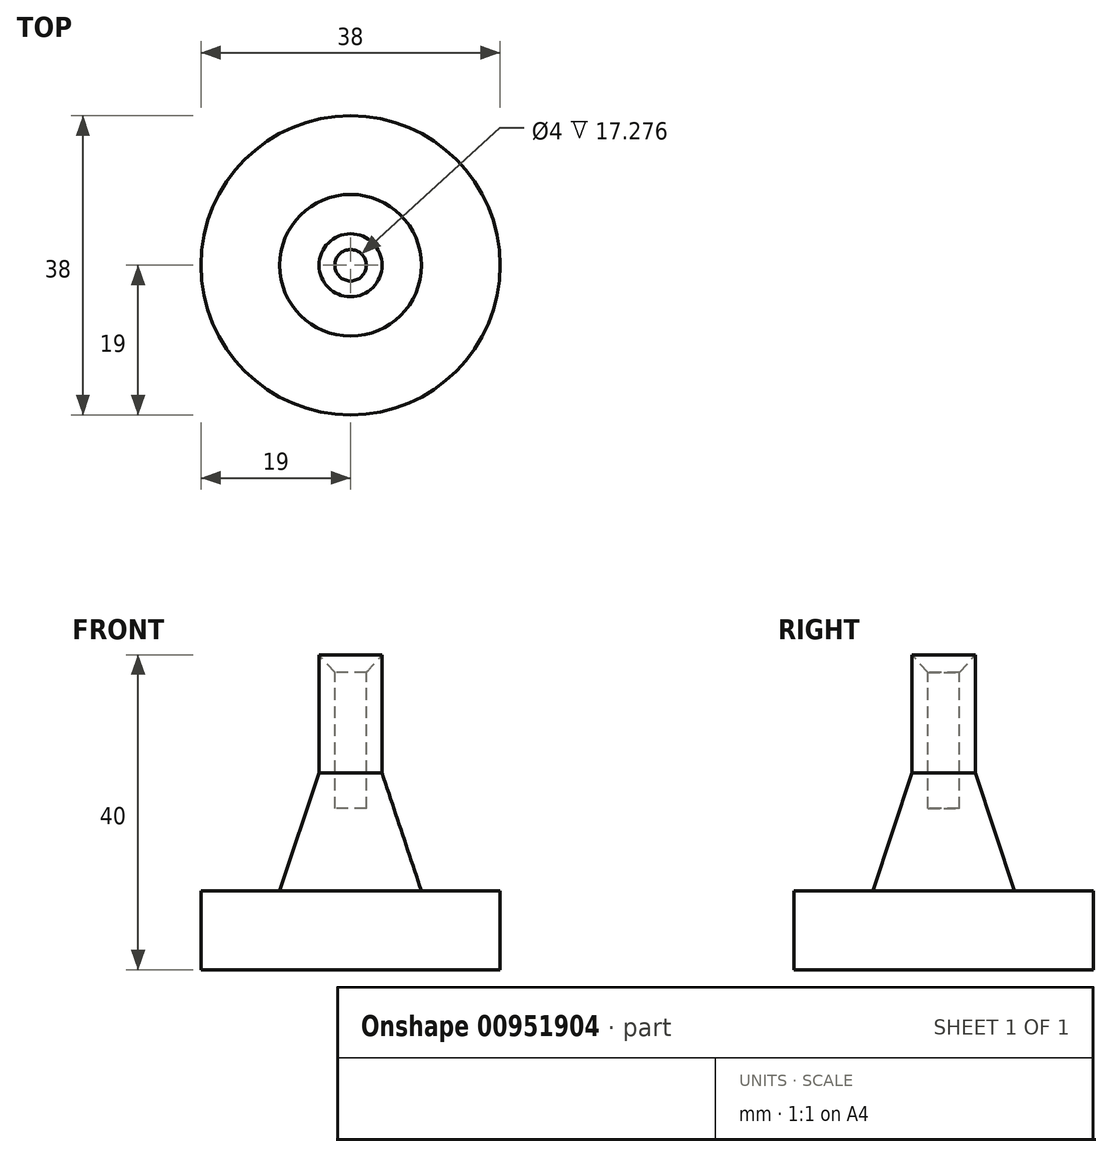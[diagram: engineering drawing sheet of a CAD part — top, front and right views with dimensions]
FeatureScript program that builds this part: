
annotation { "Feature Type Name" : "Feature", "Feature Type Description" : "" }
export const myFeature = defineFeature(function(context is Context, id is Id, definition is map)
    precondition{}
    {
        {
            var Q0;
            Q0=qCreatedBy(makeId("Front.planeOp"),FACE);
            var sketch = newSketch(context, id + "F0", { "sketchPlane" : qUnion([Q0])});
            skLineSegment(sketch, "E0", {"start": v(-4, 35.95) * mm, "end": v(-4, 20.95) * mm});
            skLineSegment(sketch, "E1", {"start": v(-9, 5.95) * mm, "end": v(-19, 5.95) * mm});
            skLineSegment(sketch, "E2", {"start": v(-19, 5.95) * mm, "end": v(-19, -4.05) * mm});
            skLineSegment(sketch, "E3", {"start": v(-19, -4.05) * mm, "end": v(0, -4.05) * mm});
            skLineSegment(sketch, "E4", {"start": v(0, 53.04) * mm, "end": v(0, 35.95) * mm, "construction": true});
            skPoint(sketch, "E4.startSnap0", {"position": v(0, 35.95) * mm});
            skPoint(sketch, "E4.endSnap0", {"position": v(0, -4.05) * mm});
            skPoint(sketch, "E5.end.orphan", {"position": v(4, 35.95) * mm});
            skPoint(sketch, "E6.end.orphan", {"position": v(3, 5.95) * mm});
            skPoint(sketch, "E7.end.orphan", {"position": v(18, 5.95) * mm});
            skPoint(sketch, "E8.orphan", {"position": v(19, -4.05) * mm});
            skLineSegment(sketch, "E9", {"start": v(0, 35.95) * mm, "end": v(0, -4.05) * mm});
            skLineSegment(sketch, "E10", {"start": v(-4, 35.95) * mm, "end": v(-2, 33.71) * mm});
            skLineSegment(sketch, "E11", {"start": v(-2, 33.71) * mm, "end": v(-2, 16.43) * mm});
            skLineSegment(sketch, "E12", {"start": v(-2, 16.43) * mm, "end": v(0, 16.43) * mm});
            skLineSegment(sketch, "E13.trimOffspring", {"start": v(0, 16.43) * mm, "end": v(0, -16.26) * mm, "construction": true});
            skLineSegment(sketch, "E14", {"start": v(-4, 20.95) * mm, "end": v(-9, 5.95) * mm});
            skPoint(sketch, "E15.orphan", {"position": v(-4, 5.95) * mm});
            skSolve(sketch);
        }
        {
            var Q0;
            Q0=makeQuery(id+"F0.imprint","IMPRINT",FACE,{"disambiguationData":[TD([[makeQuery(id+"F0.imprint","IMPRINT",EDGE,{"derivedFrom":sQuery(id+"F0.wireOp",EDGE,"E0")}),1.0]])]});
            var Q1;
            Q1=sQuery(id+"F0.wireOp",EDGE,"E9");
            revolve(context, id + "F1", {"surfaceOperationType" : NewSurfaceOperationType.NEW, "entities" : qUnion([Q0]), "axis" : qUnion([Q1]), "revolveType" : RevolveType.FULL});
        }
    });
